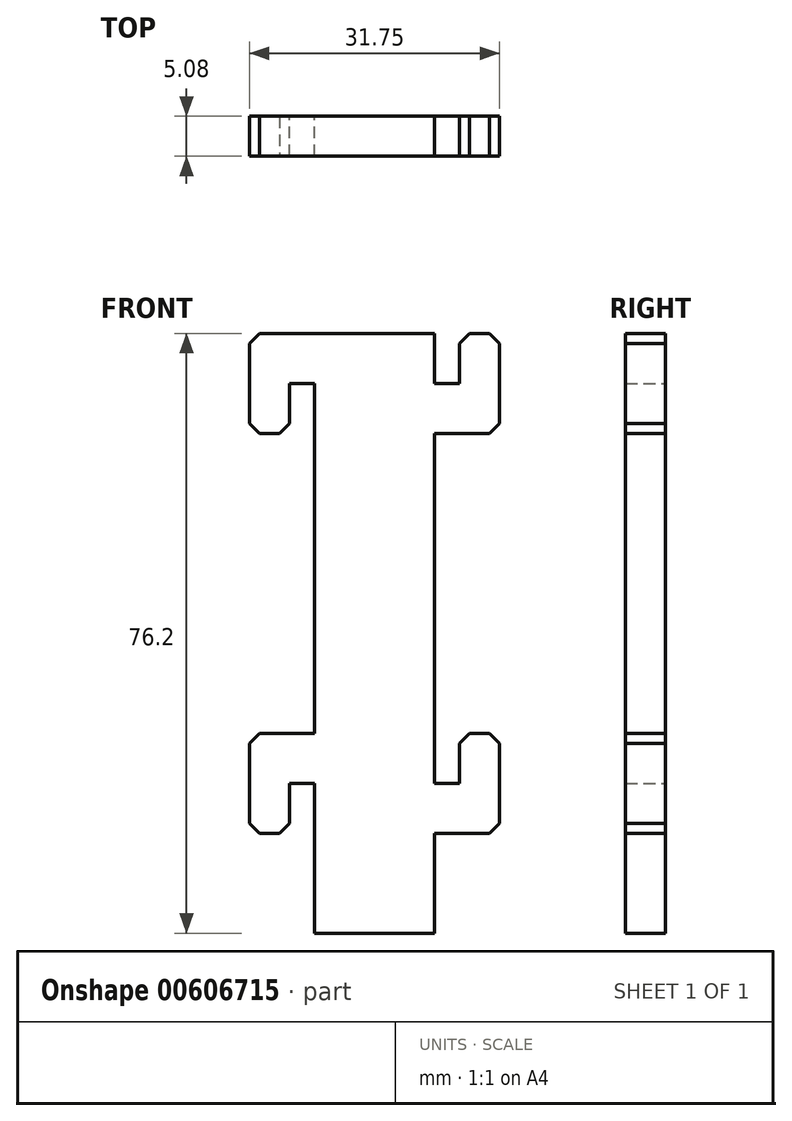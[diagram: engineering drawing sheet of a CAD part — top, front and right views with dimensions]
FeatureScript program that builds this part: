
annotation { "Feature Type Name" : "Feature", "Feature Type Description" : "" }
export const myFeature = defineFeature(function(context is Context, id is Id, definition is map)
    precondition{}
    {
        {
            var Q0;
            Q0=qCreatedBy(makeId("Front.planeOp"),FACE);
            var sketch = newSketch(context, id + "F0", { "sketchPlane" : qUnion([Q0])});
            skLineSegment(sketch, "E0", {"start": v(0, 0) * mm, "end": v(3.18, 0) * mm});
            skLineSegment(sketch, "E1", {"start": v(3.18, 0) * mm, "end": v(3.18, -50.8) * mm});
            skLineSegment(sketch, "E2", {"start": v(3.18, -50.8) * mm, "end": v(0, -50.8) * mm});
            skLineSegment(sketch, "E3", {"start": v(-47.3, -6.54) * mm, "end": v(-39.67, -6.54) * mm});
            skLineSegment(sketch, "E4", {"start": v(-39.67, -6.54) * mm, "end": v(-39.67, -19.24) * mm});
            skLineSegment(sketch, "E5", {"start": v(-39.67, -19.24) * mm, "end": v(-44.75, -19.24) * mm});
            skLineSegment(sketch, "E6", {"start": v(-44.75, -19.24) * mm, "end": v(-44.75, -12.89) * mm});
            skLineSegment(sketch, "E7", {"start": v(-44.75, -12.89) * mm, "end": v(-47.3, -12.89) * mm});
            skLineSegment(sketch, "E8", {"start": v(0, 0) * mm, "end": v(0, -6.35) * mm});
            skLineSegment(sketch, "E9", {"start": v(0, -6.35) * mm, "end": v(-5.08, -6.35) * mm});
            skLineSegment(sketch, "E10", {"start": v(-5.08, -6.35) * mm, "end": v(-5.08, 6.35) * mm});
            skLineSegment(sketch, "E11", {"start": v(-5.08, 6.35) * mm, "end": v(3.18, 6.35) * mm});
            skLineSegment(sketch, "E12", {"start": v(3.18, 6.35) * mm, "end": v(18.41, 6.35) * mm});
            skLineSegment(sketch, "E13", {"start": v(18.41, 6.35) * mm, "end": v(18.41, -69.85) * mm});
            skLineSegment(sketch, "E14", {"start": v(18.41, -69.85) * mm, "end": v(0, -69.85) * mm});
            skLineSegment(sketch, "E15", {"start": v(0, -50.8) * mm, "end": v(0, -57.15) * mm});
            skLineSegment(sketch, "E16", {"start": v(0, -57.15) * mm, "end": v(-5.08, -57.15) * mm});
            skLineSegment(sketch, "E17", {"start": v(-5.08, -57.15) * mm, "end": v(-5.08, -44.45) * mm});
            skLineSegment(sketch, "E18", {"start": v(-5.08, -44.45) * mm, "end": v(3.17, -44.45) * mm});
            skLineSegment(sketch, "E19", {"start": v(3.17, -44.45) * mm, "end": v(3.17, -69.85) * mm});
            skLineSegment(sketch, "E20", {"start": v(18.41, 0) * mm, "end": v(21.6, 0) * mm});
            skLineSegment(sketch, "E21", {"start": v(21.6, 0) * mm, "end": v(21.6, 6.35) * mm});
            skLineSegment(sketch, "E22", {"start": v(21.6, 6.35) * mm, "end": v(26.67, 6.35) * mm});
            skLineSegment(sketch, "E23", {"start": v(26.67, 6.35) * mm, "end": v(26.67, -6.35) * mm});
            skLineSegment(sketch, "E24", {"start": v(26.67, -6.35) * mm, "end": v(18.41, -6.35) * mm});
            skLineSegment(sketch, "E25", {"start": v(0.93, -50.8) * mm, "end": v(18.41, -50.8) * mm});
            skLineSegment(sketch, "E26", {"start": v(18.41, -50.8) * mm, "end": v(21.6, -50.8) * mm});
            skLineSegment(sketch, "E27", {"start": v(21.6, -50.8) * mm, "end": v(21.6, -44.45) * mm});
            skLineSegment(sketch, "E28", {"start": v(21.6, -44.45) * mm, "end": v(26.67, -44.45) * mm});
            skLineSegment(sketch, "E29", {"start": v(26.67, -44.45) * mm, "end": v(26.67, -57.15) * mm});
            skLineSegment(sketch, "E30", {"start": v(26.67, -57.15) * mm, "end": v(18.41, -57.15) * mm});
            skSolve(sketch);
        }
        {
            var Q0;
            Q0 = qSketchRegion(id + "F0", true);
            extrude(context, id + "F1", {"entities" : qUnion([Q0]), "depth" : 5.08 * mm, "offsetDistance" : 25.4 * mm});
        }
        {
            var Q0;
            Q0=makeQuery(id+"F1.opExtrude","SWEPT_EDGE",EDGE,{"disambiguationData":[OSD([sQuery(id+"F0.wireOp",EDGE,"E21"),sQuery(id+"F0.wireOp",EDGE,"E22")])]});
            var Q1;
            Q1=makeQuery(id+"F1.opExtrude","SWEPT_EDGE",EDGE,{"disambiguationData":[OSD([sQuery(id+"F0.wireOp",EDGE,"E22"),sQuery(id+"F0.wireOp",EDGE,"E23")])]});
            var Q2;
            Q2=makeQuery(id+"F1.opExtrude","SWEPT_EDGE",EDGE,{"disambiguationData":[OSD([sQuery(id+"F0.wireOp",EDGE,"E23"),sQuery(id+"F0.wireOp",EDGE,"E24")])]});
            var Q3;
            Q3=makeQuery(id+"F1.opExtrude","SWEPT_EDGE",EDGE,{"disambiguationData":[OSD([sQuery(id+"F0.wireOp",EDGE,"E8"),sQuery(id+"F0.wireOp",EDGE,"E9")])]});
            var Q4;
            Q4=makeQuery(id+"F1.opExtrude","SWEPT_EDGE",EDGE,{"disambiguationData":[OSD([sQuery(id+"F0.wireOp",EDGE,"E9"),sQuery(id+"F0.wireOp",EDGE,"E10")])]});
            var Q5;
            Q5=makeQuery(id+"F1.opExtrude","SWEPT_EDGE",EDGE,{"disambiguationData":[OSD([sQuery(id+"F0.wireOp",EDGE,"E10"),sQuery(id+"F0.wireOp",EDGE,"E11")])]});
            var Q6;
            Q6=makeQuery(id+"F1.opExtrude","SWEPT_EDGE",EDGE,{"disambiguationData":[OSD([sQuery(id+"F0.wireOp",EDGE,"E28"),sQuery(id+"F0.wireOp",EDGE,"E29")])]});
            var Q7;
            Q7=makeQuery(id+"F1.opExtrude","SWEPT_EDGE",EDGE,{"disambiguationData":[OSD([sQuery(id+"F0.wireOp",EDGE,"E27"),sQuery(id+"F0.wireOp",EDGE,"E28")])]});
            var Q8;
            Q8=makeQuery(id+"F1.opExtrude","SWEPT_EDGE",EDGE,{"disambiguationData":[OSD([sQuery(id+"F0.wireOp",EDGE,"E29"),sQuery(id+"F0.wireOp",EDGE,"E30")])]});
            var Q9;
            Q9=makeQuery(id+"F1.opExtrude","SWEPT_EDGE",EDGE,{"disambiguationData":[OSD([sQuery(id+"F0.wireOp",EDGE,"E17"),sQuery(id+"F0.wireOp",EDGE,"E18")])]});
            var Q10;
            Q10=makeQuery(id+"F1.opExtrude","SWEPT_EDGE",EDGE,{"disambiguationData":[OSD([sQuery(id+"F0.wireOp",EDGE,"E16"),sQuery(id+"F0.wireOp",EDGE,"E17")])]});
            var Q11;
            Q11=makeQuery(id+"F1.opExtrude","SWEPT_EDGE",EDGE,{"disambiguationData":[OSD([sQuery(id+"F0.wireOp",EDGE,"E15"),sQuery(id+"F0.wireOp",EDGE,"E16")])]});
            chamfer(context, id + "F2", {"entities" : qUnion([Q0, Q1, Q2, Q3, Q4, Q5, Q6, Q7, Q8, Q9, Q10, Q11]), "width" : 1.27 * mm, "tangentPropagation" : true});
        }
    });
